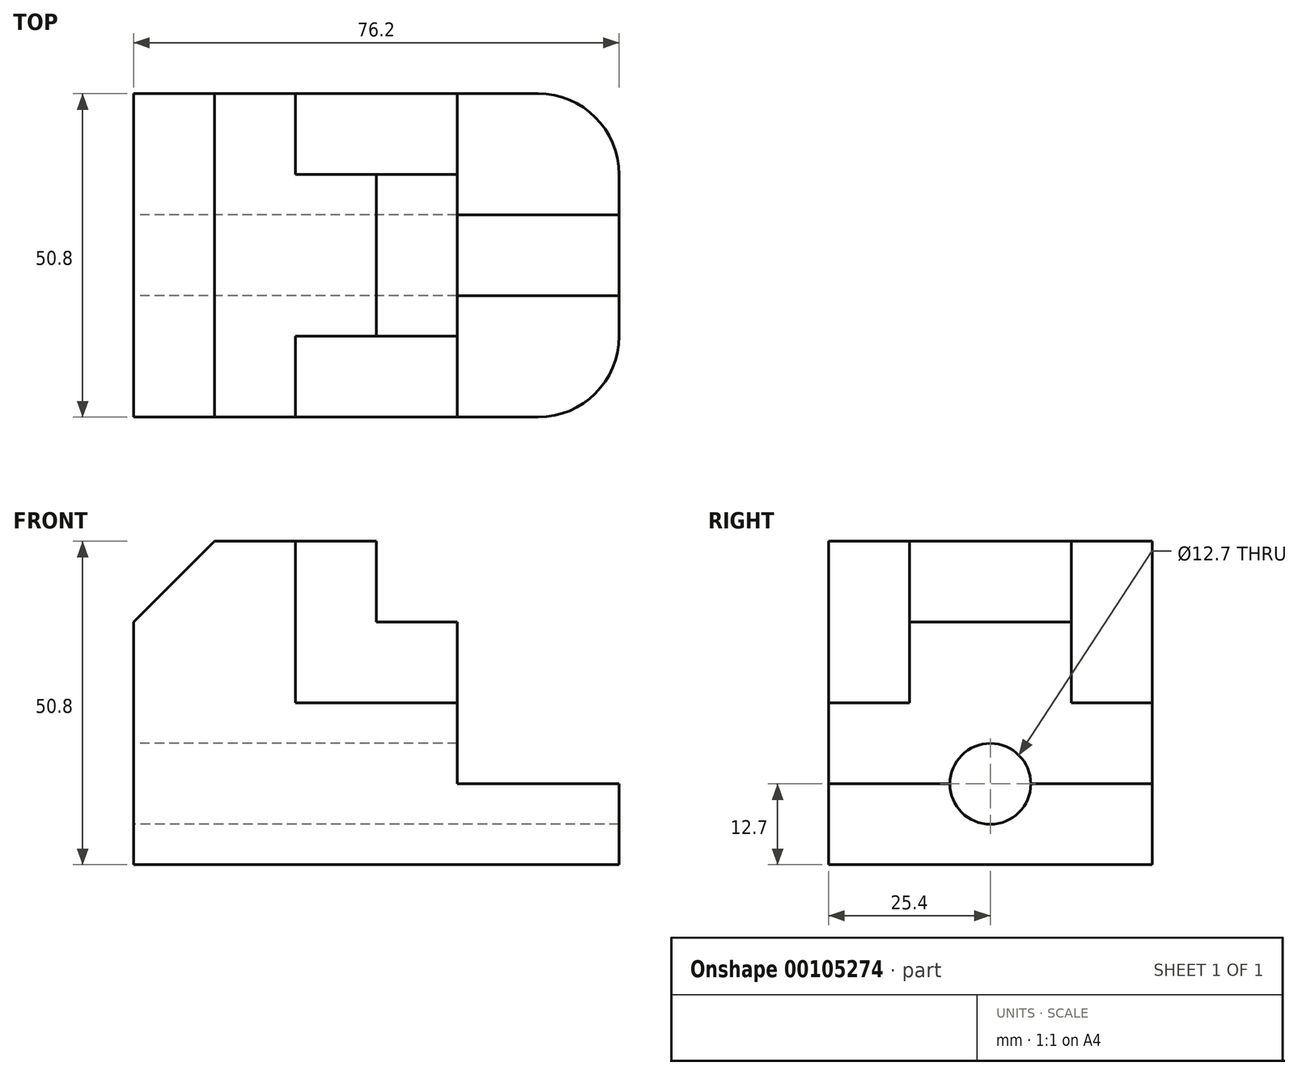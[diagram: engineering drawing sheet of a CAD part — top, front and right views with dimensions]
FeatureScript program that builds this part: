
annotation { "Feature Type Name" : "Feature", "Feature Type Description" : "" }
export const myFeature = defineFeature(function(context is Context, id is Id, definition is map)
    precondition{}
    {
        {
            var Q0;
            Q0=qCreatedBy(makeId("Front.planeOp"),FACE);
            var sketch = newSketch(context, id + "F0", { "sketchPlane" : qUnion([Q0])});
            skLineSegment(sketch, "E0.bottom", {"start": v(0, 0) * mm, "end": v(76.2, 0) * mm});
            skLineSegment(sketch, "E0.top", {"start": v(12.7, 50.8) * mm, "end": v(38.1, 50.8) * mm});
            skLineSegment(sketch, "E0.left", {"start": v(0, 0) * mm, "end": v(0, 38.1) * mm});
            skLineSegment(sketch, "E0.right", {"start": v(76.2, 0) * mm, "end": v(76.2, 12.7) * mm});
            skLineSegment(sketch, "E1.top", {"start": v(76.2, 12.7) * mm, "end": v(50.8, 12.7) * mm});
            skLineSegment(sketch, "E1.right", {"start": v(50.8, 38.1) * mm, "end": v(50.8, 12.7) * mm});
            skLineSegment(sketch, "E2.top", {"start": v(50.8, 38.1) * mm, "end": v(38.1, 38.1) * mm});
            skLineSegment(sketch, "E2.right", {"start": v(38.1, 50.8) * mm, "end": v(38.1, 38.1) * mm});
            skPoint(sketch, "E3.orphan", {"position": v(50.8, 50.8) * mm});
            skLineSegment(sketch, "E4", {"start": v(0, 38.1) * mm, "end": v(12.7, 50.8) * mm});
            skPoint(sketch, "E5.orphan", {"position": v(0, 50.8) * mm});
            skSolve(sketch);
        }
        {
            var Q0;
            Q0 = qSketchRegion(id + "F0", true);
            extrude(context, id + "F1", {"entities" : qUnion([Q0]), "endBound" : BoundingType.SYMMETRIC, "depth" : 50.8 * mm});
        }
        {
            var Q0;
            Q0=makeQuery(id+"F1.opExtrude","CAP_FACE",FACE,{"disambiguationData":[OSD([sQuery(id+"F0.wireOp",EDGE,"E0.bottom"),sQuery(id+"F0.wireOp",EDGE,"E0.top"),sQuery(id+"F0.wireOp",EDGE,"E0.left"),sQuery(id+"F0.wireOp",EDGE,"E0.right"),sQuery(id+"F0.wireOp",EDGE,"E1.top"),sQuery(id+"F0.wireOp",EDGE,"E1.right"),sQuery(id+"F0.wireOp",EDGE,"E2.top"),sQuery(id+"F0.wireOp",EDGE,"E2.right"),sQuery(id+"F0.wireOp",EDGE,"E4")])],"isStart":false});
            var sketch = newSketch(context, id + "F2", { "sketchPlane" : qUnion([Q0])});
            skLineSegment(sketch, "E6.bottom", {"start": v(25.4, 50.8) * mm, "end": v(50.8, 50.8) * mm});
            skLineSegment(sketch, "E6.top", {"start": v(25.4, 25.4) * mm, "end": v(50.8, 25.4) * mm});
            skLineSegment(sketch, "E6.left", {"start": v(25.4, 50.8) * mm, "end": v(25.4, 25.4) * mm});
            skLineSegment(sketch, "E6.right", {"start": v(50.8, 50.8) * mm, "end": v(50.8, 25.4) * mm});
            skSolve(sketch);
        }
        {
            var Q0;
            {var subQ2=sQuery(id+"F2.wireOp",EDGE,"E6.top");Q0=makeQuery(id+"F2.imprint","IMPRINT",FACE,{"disambiguationData":[TD([[makeQuery(id+"F2.imprint","IMPRINT",EDGE,{"derivedFrom":subQ2}),1.0]])]});}
            extrude(context, id + "F3", {"entities" : qUnion([Q0]), "operationType" : NewBodyOperationType.REMOVE, "oppositeDirection" : true, "depth" : 12.7 * mm});
        }
        {
            var Q0;
            Q0=makeQuery(id+"F1.opExtrude","CAP_FACE",FACE,{"disambiguationData":[OSD([sQuery(id+"F0.wireOp",EDGE,"E0.bottom"),sQuery(id+"F0.wireOp",EDGE,"E0.top"),sQuery(id+"F0.wireOp",EDGE,"E0.left"),sQuery(id+"F0.wireOp",EDGE,"E0.right"),sQuery(id+"F0.wireOp",EDGE,"E1.top"),sQuery(id+"F0.wireOp",EDGE,"E1.right"),sQuery(id+"F0.wireOp",EDGE,"E2.top"),sQuery(id+"F0.wireOp",EDGE,"E2.right"),sQuery(id+"F0.wireOp",EDGE,"E4")])],"isStart":true});
            var sketch = newSketch(context, id + "F4", { "sketchPlane" : qUnion([Q0])});
            skPoint(sketch, "E7.firstSnap0", {"position": v(-25.4, 50.8) * mm});
            skPoint(sketch, "E7.oppositeSnap0", {"position": v(-25.4, 50.8) * mm});
            skLineSegment(sketch, "E7.bottom", {"start": v(-50.8, 50.8) * mm, "end": v(-25.4, 50.8) * mm});
            skLineSegment(sketch, "E7.top", {"start": v(-50.8, 25.4) * mm, "end": v(-25.4, 25.4) * mm});
            skLineSegment(sketch, "E7.left", {"start": v(-50.8, 50.8) * mm, "end": v(-50.8, 25.4) * mm});
            skLineSegment(sketch, "E7.right", {"start": v(-25.4, 50.8) * mm, "end": v(-25.4, 25.4) * mm});
            skSolve(sketch);
        }
        {
            var Q0;
            {var subQ2=sQuery(id+"F4.wireOp",EDGE,"E7.top");Q0=makeQuery(id+"F4.imprint","IMPRINT",FACE,{"disambiguationData":[TD([[makeQuery(id+"F4.imprint","IMPRINT",EDGE,{"derivedFrom":subQ2}),1.0]])]});}
            extrude(context, id + "F5", {"entities" : qUnion([Q0]), "operationType" : NewBodyOperationType.REMOVE, "oppositeDirection" : true, "depth" : 12.7 * mm});
        }
        {
            var Q0;
            Q0=makeQuery(id+"F1.opExtrude","SWEPT_FACE",FACE,{"disambiguationData":[OSD([sQuery(id+"F0.wireOp",EDGE,"E0.left")])]});
            var sketch = newSketch(context, id + "F6", { "sketchPlane" : qUnion([Q0])});
            skCircle(sketch, "E8", {"center": v(0, 12.7) * mm, "radius": 6.35 * mm});
            skSolve(sketch);
        }
        {
            var Q0;
            Q0=makeQuery(id+"F6.imprint","IMPRINT",FACE,{"disambiguationData":[TD([[makeQuery(id+"F6.imprint","IMPRINT",EDGE,{"derivedFrom":sQuery(id+"F6.wireOp",EDGE,"E8")}),1.0]])]});
            extrude(context, id + "F7", {"entities" : qUnion([Q0]), "operationType" : NewBodyOperationType.REMOVE, "endBound" : BoundingType.THROUGH_ALL, "oppositeDirection" : true, "depth" : 25.4 * mm});
        }
        {
            var Q0;
            Q0=makeQuery(id+"F1.opExtrude","CAP_EDGE",EDGE,{"disambiguationData":[OSD([sQuery(id+"F0.wireOp",EDGE,"E0.right")])],"isStart":true});
            var Q1;
            Q1=makeQuery(id+"F1.opExtrude","CAP_EDGE",EDGE,{"disambiguationData":[OSD([sQuery(id+"F0.wireOp",EDGE,"E0.right")])],"isStart":false});
            fillet(context, id + "F8", {"entities" : qUnion([Q0, Q1]), "radius" : 12.7 * mm, "tangentPropagation" : true, "allowEdgeOverflow" : false});
        }
    });
